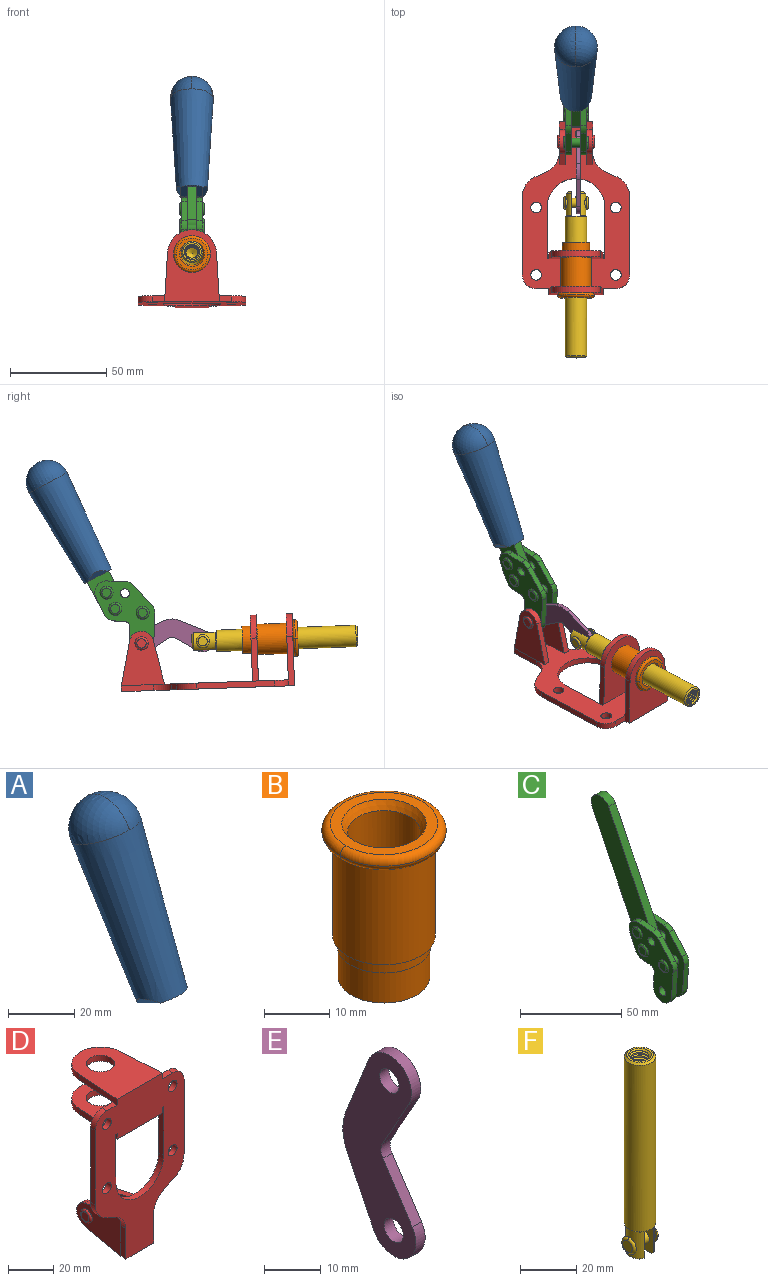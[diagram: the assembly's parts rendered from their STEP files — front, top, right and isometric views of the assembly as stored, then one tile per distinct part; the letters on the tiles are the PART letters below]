
ASSEMBLY  parts=6 mates=6
PART A: 11 faces, bbox 22.3x42.6x64.5 mm
  f0: sphere r=11.13mm, area 411.4mm2, adj f1,f8
  f1: cone r=11.11mm half-angle=3.3deg, axis (0,0.44,0.9), area 3251.8mm2, adj f0,f7,f8,f9,f10
  f2: cylinder r=6.16mm len=11.7mm, axis (1,0,0), area 89.5mm2, adj f3,f4,f5,f6
  f3: plane 60.23x36.75mm, normal (-1,0,0), area 763.6mm2, adj f2,f4,f6,f10
  f4: plane 51.37x25.05mm, normal (0,0.9,-0.44), area 264.2mm2, adj f2,f3,f5,f10
  f5: plane 60.23x36.75mm, normal (1,0,0), area 763.6mm2, adj f2,f4,f6,f10
  f6: plane 51.37x25.05mm, normal (0,-0.9,0.44), area 264.2mm2, adj f2,f3,f5,f10
  f7: plane 9.95x5.95mm, normal (0.71,-0.31,-0.64), area 25.8mm2, adj f1,f10
  f8: sphere r=11.13mm, area 411.4mm2, adj f0,f1
  f9: plane 9.95x5.95mm, normal (-0.71,-0.31,-0.64), area 25.8mm2, adj f1,f10
  f10: plane 14.27x11.38mm, normal (0,-0.44,-0.9), area 106.7mm2, adj f1,f3,f4,f5,f6,f7,f9
PART B: 15 faces, bbox 20.6x20.6x28.7 mm
  f0: torus R=8.26mm, axis (0,0,1), area 56.8mm2, adj f1,f10,f12
  f1: torus R=8.26mm, axis (0,0,1), area 56.8mm2, adj f0,f6,f13
  f2: cylinder r=5.59mm len=25.91mm, axis (0,0,1), area 909.6mm2, adj f3,f4
  f3: cone r=6.86mm half-angle=45deg, axis (0,0,-1), area 70.2mm2, adj f2,f14
  f4: cone r=6.47mm half-angle=30deg, axis (0,0,1), area 66.7mm2, adj f2,f13
  f5: cylinder r=7.04mm len=14.07mm, axis (0,0,1), area 252.6mm2, adj f11,f14
  f6: torus R=8.26mm, axis (0,0,1), area 56.8mm2, adj f1,f12,f13
  f7: cylinder r=7.16mm len=14.33mm, axis (0,0,1), area 91.5mm2, adj f9,f11
  f8: cylinder r=7.86mm len=18.42mm, axis (0,0,1), area 909.6mm2, adj f9,f10
  f9: plane 15.72x15.72mm, normal (0,0,-1), area 33mm2, adj f7,f8
  f10: plane 16.51x16.51mm, normal (0,0,-1), area 19.9mm2, adj f0,f8,f12
  f11: plane 14.33x14.33mm, normal (0,0,-1), area 5.7mm2, adj f5,f7
  f12: torus R=8.26mm, axis (0,0,1), area 56.8mm2, adj f0,f6,f10
  f13: plane 16.51x16.51mm, normal (0,0,1), area 82.7mm2, adj f1,f4,f6
  f14: plane 14.07x14.07mm, normal (0,0,-1), area 7.8mm2, adj f3,f5
PART C: 59 faces, bbox 12.9x60.2x99.6 mm
  f0: torus R=2.39mm, axis (-1,0,0), area 14.9mm2, adj f20,f43,f51
  f1: torus R=2.39mm, axis (-1,0,0), area 14.9mm2, adj f19,f42,f51
  f2: torus R=2.39mm, axis (-1,0,0), area 14.9mm2, adj f18,f35,f51
  f3: torus R=2.39mm, axis (-1,0,0), area 14.9mm2, adj f14,f17,f23
  f4: torus R=2.39mm, axis (-1,0,0), area 14.9mm2, adj f13,f16,f23
  f5: torus R=2.39mm, axis (-1,0,0), area 14.9mm2, adj f12,f15,f23
  f6: cylinder r=2.39mm len=4.78mm, axis (1,0,0), area 46.5mm2, adj f48,f50,f51
  f7: cylinder r=2.39mm len=4.78mm, axis (1,0,0), area 46.5mm2, adj f50,f51
  f8: cylinder r=6.35mm len=12.68mm, axis (1,0,0), area 61.8mm2, adj f38,f39,f50,f51
  f9: cylinder r=2.39mm len=4.78mm, axis (-1,0,0), area 70.5mm2, adj f46,f50
  f10: cylinder r=2.39mm len=4.78mm, axis (-1,0,0), area 46.5mm2, adj f23,f45,f46
  f11: cylinder r=2.39mm len=4.78mm, axis (-1,0,0), area 46.5mm2, adj f23,f46
  f12: plane 4.78x4.78mm, normal (1,0,0), area 17.9mm2, adj f5,f15
  f13: plane 4.78x4.78mm, normal (1,0,0), area 17.9mm2, adj f4,f16
  f14: plane 4.78x4.78mm, normal (1,0,0), area 17.9mm2, adj f3,f17
  f15: torus R=2.39mm, axis (-1,0,0), area 14.9mm2, adj f5,f12,f23
  f16: torus R=2.39mm, axis (-1,0,0), area 14.9mm2, adj f4,f13,f23
  f17: torus R=2.39mm, axis (-1,0,0), area 14.9mm2, adj f3,f14,f23
  f18: plane 4.78x4.78mm, normal (-1,0,0), area 17.9mm2, adj f2,f35
  f19: plane 4.78x4.78mm, normal (-1,0,0), area 17.9mm2, adj f1,f42
  f20: plane 4.78x4.78mm, normal (-1,0,0), area 17.9mm2, adj f0,f43
  f21: plane 2.26x0.2mm, normal (1,0,0), area 0.2mm2, adj f31,f44
  f22: plane 2.26x0.2mm, normal (-1,0,0), area 0.2mm2, adj f41,f44
  f23: plane 39.37x30.77mm, normal (1,0,0), area 565.5mm2, adj f3,f4,f5,f10,f11,f15,f16,f17
  f24: cylinder r=6.1mm len=4.15mm, axis (-1,0,0), area 14.7mm2, adj f23,f25,f32,f46
  f25: plane 10.25x9.01mm, normal (0,-0.75,0.66), area 42.3mm2, adj f23,f24,f26,f46
  f26: cylinder r=6.35mm len=4.64mm, axis (-1,0,0), area 15.6mm2, adj f23,f25,f27,f46
  f27: plane 15.84x3.1mm, normal (0,-1,-0.07), area 49.2mm2, adj f23,f26,f28,f46
  f28: cylinder r=6.35mm len=12.68mm, axis (-1,0,0), area 61.8mm2, adj f23,f27,f29,f46
  f29: plane 8.11x3.1mm, normal (0,1,0.07), area 25.2mm2, adj f23,f28,f30,f46
  f30: cylinder r=3.05mm len=3.25mm, axis (-1,0,0), area 14.8mm2, adj f23,f29,f31,f46
  f31: plane 5.99x3.1mm, normal (0,0.07,-1), area 18.6mm2, adj f21,f23,f30,f44,f46
  f32: plane 9.5x3.1mm, normal (0,-0.07,1), area 29.5mm2, adj f23,f24,f33,f46,f47
  f33: cylinder r=6.1mm len=8.63mm, axis (-1,0,0), area 39.1mm2, adj f23,f32,f34,f47
  f34: plane 8.65x3.96mm, normal (0,0.91,-0.42), area 29.5mm2, adj f23,f33,f44,f47
  f35: torus R=2.39mm, axis (-1,0,0), area 14.9mm2, adj f2,f18,f51
  f36: plane 10.25x9.01mm, normal (0,-0.75,0.66), area 42.3mm2, adj f37,f49,f50,f51
  f37: cylinder r=6.35mm len=4.64mm, axis (1,0,0), area 15.6mm2, adj f36,f38,f50,f51
  f38: plane 15.84x3.1mm, normal (0,-1,-0.07), area 49.2mm2, adj f8,f37,f50,f51
  f39: plane 8.11x3.1mm, normal (0,1,0.07), area 25.2mm2, adj f8,f40,f50,f51
  f40: cylinder r=3.05mm len=3.25mm, axis (1,0,0), area 14.8mm2, adj f39,f41,f50,f51
  f41: plane 5.99x3.1mm, normal (0,0.07,-1), area 18.6mm2, adj f22,f40,f44,f50,f51
  f42: torus R=2.39mm, axis (-1,0,0), area 14.9mm2, adj f1,f19,f51
  f43: torus R=2.39mm, axis (-1,0,0), area 14.9mm2, adj f0,f20,f51
  f44: cylinder r=6.35mm len=12.12mm, axis (-1,0,0), area 128.9mm2, adj f21,f22,f23,f31,f34,f41,f46,f47
  f45: plane 2.65x1.35mm, normal (1,0,0), area 1mm2, adj f10,f55
  f46: plane 39.08x20.42mm, normal (-1,0,0), area 412.5mm2, adj f9,f10,f11,f24,f25,f26,f27,f28
  f47: plane 77.62x39.82mm, normal (1,0,0), area 850mm2, adj f32,f33,f34,f44,f53,f54,f55
  f48: plane 2.65x1.35mm, normal (-1,0,0), area 1mm2, adj f6,f55
  f49: cylinder r=6.1mm len=4.15mm, axis (1,0,0), area 14.7mm2, adj f36,f50,f51,f56
  f50: plane 39.08x20.42mm, normal (1,0,0), area 412.5mm2, adj f6,f7,f8,f9,f36,f37,f38,f39
  f51: plane 39.37x30.77mm, normal (-1,0,0), area 565.5mm2, adj f0,f1,f2,f6,f7,f8,f35,f36
  f52: plane 8.65x3.96mm, normal (0,0.91,-0.42), area 29.5mm2, adj f44,f51,f57,f58
  f53: plane 68.49x33.4mm, normal (0,0.9,-0.44), area 358.1mm2, adj f44,f47,f54,f58
  f54: cylinder r=6.35mm len=12.06mm, axis (1,0,0), area 93.7mm2, adj f47,f53,f55,f58
  f55: plane 68.49x33.4mm, normal (0,-0.9,0.44), area 358.1mm2, adj f44,f45,f46,f47,f48,f50,f54,f58
  f56: plane 9.5x3.1mm, normal (0,-0.07,1), area 29.5mm2, adj f49,f50,f51,f57,f58
  f57: cylinder r=6.1mm len=8.63mm, axis (1,0,0), area 39.1mm2, adj f51,f52,f56,f58
  f58: plane 77.62x39.82mm, normal (-1,0,0), area 850mm2, adj f44,f52,f53,f54,f55,f56,f57
PART D: 55 faces, bbox 55.7x37.4x89.8 mm
  f0: torus R=2.41mm, axis (-1,0,0), area 15mm2, adj f11,f15,f25
  f1: torus R=2.41mm, axis (-1,0,0), area 15mm2, adj f10,f12,f22
  f2: cylinder r=2.78mm len=5.56mm, axis (0,-1,0), area 54.2mm2, adj f30,f54
  f3: cylinder r=14.99mm len=29.97mm, axis (0,-1,0), area 145.9mm2, adj f30,f49,f53,f54
  f4: cylinder r=2.78mm len=5.56mm, axis (0,-1,0), area 54.2mm2, adj f30,f54
  f5: cylinder r=2.78mm len=5.56mm, axis (0,-1,0), area 54.2mm2, adj f30,f54
  f6: cylinder r=2.78mm len=5.56mm, axis (0,-1,0), area 54.2mm2, adj f30,f54
  f7: cylinder r=6.35mm len=12.7mm, axis (0,0,1), area 123.6mm2, adj f27,f51
  f8: cylinder r=6.35mm len=12.7mm, axis (0,0,-1), area 124.7mm2, adj f21,f35
  f9: cylinder r=2.41mm len=11.18mm, axis (-1,0,0), area 169.4mm2, adj f16,f19
  f10: plane 4.83x4.83mm, normal (1,0,0), area 18.3mm2, adj f1,f12
  f11: plane 4.83x4.83mm, normal (-1,0,0), area 18.3mm2, adj f0,f15
  f12: torus R=2.41mm, axis (-1,0,0), area 15mm2, adj f1,f10,f22
  f13: cylinder r=6.35mm len=12.41mm, axis (1,0,0), area 53.4mm2, adj f18,f19,f22,f23
  f14: cylinder r=6.35mm len=12.41mm, axis (-1,0,0), area 53.4mm2, adj f16,f17,f24,f25
  f15: torus R=2.41mm, axis (-1,0,0), area 15mm2, adj f0,f11,f25
  f16: plane 27.86x22.35mm, normal (1,0,0), area 425.4mm2, adj f9,f14,f17,f24,f30
  f17: plane 22.86x4.97mm, normal (0,0.21,0.98), area 72.5mm2, adj f14,f16,f25,f30
  f18: plane 22.86x4.97mm, normal (0,0.21,0.98), area 72.5mm2, adj f13,f19,f22,f30
  f19: plane 27.86x22.35mm, normal (-1,0,0), area 425.4mm2, adj f9,f13,f18,f23,f30
  f20: cylinder r=12.7mm len=25.35mm, axis (0,0,-1), area 119.8mm2, adj f21,f34,f35,f36
  f21: plane 34.21x28.07mm, normal (0,0,-1), area 702.4mm2, adj f8,f20,f30,f34,f36
  f22: plane 27.96x22.45mm, normal (1,0,0), area 407.2mm2, adj f1,f12,f13,f18,f23,f30,f42,f43
  f23: plane 22.86x4.97mm, normal (0,0.21,-0.98), area 72.5mm2, adj f13,f19,f22,f44
  f24: plane 22.86x4.97mm, normal (0,0.21,-0.98), area 72.5mm2, adj f14,f16,f25,f44
  f25: plane 27.86x22.35mm, normal (-1,0,0), area 407.1mm2, adj f0,f14,f15,f17,f24,f30,f45,f46
  f26: plane 3.1x0.95mm, normal (0,0,-1), area 2.7mm2, adj f30,f49,f50,f54
  f27: plane 34.21x28.07mm, normal (0,0,1), area 702.4mm2, adj f7,f28,f30,f50,f52
  f28: cylinder r=12.7mm len=25.35mm, axis (0,0,1), area 118.8mm2, adj f27,f50,f51,f52
  f29: plane 3.1x0.95mm, normal (0,0,-1), area 2.7mm2, adj f30,f52,f53,f54
  f30: plane 86.54x55.63mm, normal (0,1,0), area 2362.9mm2, adj f2,f3,f4,f5,f6,f16,f17,f18
  f31: plane 40.56x3.1mm, normal (-1,0,0), area 125.7mm2, adj f30,f32,f48,f54
  f32: cylinder r=7.11mm len=7.11mm, axis (0,-1,0), area 34.6mm2, adj f30,f31,f33,f54
  f33: plane 6.67x3.1mm, normal (0,0,1), area 20.4mm2, adj f30,f32,f34,f54
  f34: plane 25.39x3.13mm, normal (-1,0.06,0), area 79.5mm2, adj f20,f21,f33,f35,f54
  f35: plane 37.31x28.45mm, normal (0,0,1), area 789.9mm2, adj f8,f20,f34,f36,f54
  f36: plane 25.39x3.13mm, normal (1,0.06,0), area 79.5mm2, adj f20,f21,f35,f37,f54
  f37: plane 6.67x3.1mm, normal (0,0,1), area 20.4mm2, adj f30,f36,f38,f54
  f38: cylinder r=7.11mm len=7.11mm, axis (0,-1,0), area 34.6mm2, adj f30,f37,f39,f54
  f39: plane 40.56x3.1mm, normal (1,0,0), area 125.7mm2, adj f30,f38,f40,f54
  f40: cylinder r=11.18mm len=10.16mm, axis (0,-1,0), area 39.5mm2, adj f30,f39,f41,f54
  f41: plane 6.09x3.1mm, normal (0.42,0,-0.91), area 20.8mm2, adj f30,f40,f42,f54
  f42: cylinder r=11.18mm len=9.41mm, axis (0,-1,0), area 37.2mm2, adj f22,f30,f41,f43,f54
  f43: plane 16.5x3.1mm, normal (1,0,0), area 51.1mm2, adj f22,f42,f44,f54
  f44: plane 17.37x3.1mm, normal (0,0,-1), area 53.8mm2, adj f23,f24,f30,f43,f45,f54
  f45: plane 16.5x3.1mm, normal (-1,0,0), area 51.1mm2, adj f25,f44,f46,f54
  f46: cylinder r=11.18mm len=9.41mm, axis (0,-1,0), area 37.2mm2, adj f25,f30,f45,f47,f54
  f47: plane 6.09x3.1mm, normal (-0.42,0,-0.91), area 20.8mm2, adj f30,f46,f48,f54
  f48: cylinder r=11.18mm len=10.16mm, axis (0,-1,0), area 39.5mm2, adj f30,f31,f47,f54
  f49: plane 26.54x3.1mm, normal (-1,0,0), area 82.3mm2, adj f3,f26,f30,f54
  f50: plane 25.39x3.1mm, normal (1,0.06,0), area 78.8mm2, adj f26,f27,f28,f51,f54
  f51: plane 37.31x28.45mm, normal (0,0,-1), area 789.9mm2, adj f7,f28,f50,f52,f54
  f52: plane 25.39x3.1mm, normal (-1,0.06,0), area 78.8mm2, adj f27,f28,f29,f51,f54
  f53: plane 26.54x3.1mm, normal (1,0,0), area 82.3mm2, adj f3,f29,f30,f54
  f54: plane 89.66x55.63mm, normal (0,-1,0), area 2678.5mm2, adj f2,f3,f4,f5,f6,f26,f29,f31
PART E: 12 faces, bbox 2.3x18.2x42.8 mm
  f0: cylinder r=2.4mm len=4.8mm, axis (1,0,0), area 34.9mm2, adj f4,f11
  f1: cylinder r=10.41mm len=8.47mm, axis (1,0,0), area 20.2mm2, adj f4,f9,f10,f11
  f2: cylinder r=3.05mm len=3.16mm, axis (1,0,0), area 7.7mm2, adj f4,f6,f7,f11
  f3: cylinder r=2.4mm len=4.8mm, axis (1,0,0), area 34.9mm2, adj f4,f11
  f4: plane 42.81x18.23mm, normal (-1,0,0), area 414.1mm2, adj f0,f1,f2,f3,f5,f6,f7,f8
  f5: cylinder r=5.54mm len=10.67mm, axis (1,0,0), area 41.8mm2, adj f4,f6,f10,f11
  f6: plane 11.66x6.53mm, normal (0,-0.87,-0.49), area 30.9mm2, adj f2,f4,f5,f11
  f7: plane 11.17x7.33mm, normal (0,-0.84,0.55), area 30.9mm2, adj f2,f4,f8,f11
  f8: cylinder r=5.54mm len=10.51mm, axis (1,0,0), area 41.8mm2, adj f4,f7,f9,f11
  f9: plane 13.67x6.67mm, normal (0,0.9,-0.44), area 35.1mm2, adj f1,f4,f8,f11
  f10: plane 14.1x5.7mm, normal (0,0.93,0.37), area 35.1mm2, adj f1,f4,f5,f11
  f11: plane 42.81x18.23mm, normal (1,0,0), area 414.1mm2, adj f0,f1,f2,f3,f5,f6,f7,f8
PART F: 48 faces, bbox 12.6x11.1x86.1 mm
  f0: torus R=2.41mm, axis (-1,0,0), area 15mm2, adj f30,f32,f34
  f1: torus R=2.41mm, axis (-1,0,0), area 15mm2, adj f29,f31,f33
  f2: cylinder r=5.54mm len=72.39mm, axis (0,0,1), area 2518.5mm2, adj f3,f4,f42,f43
  f3: cone r=5.54mm half-angle=45deg, axis (0,0,1), area 7.6mm2, adj f2,f5,f41
  f4: cone r=5.54mm half-angle=45deg, axis (0,0,-1), area 34.9mm2, adj f2,f39
  f5: cylinder r=5.08mm len=11.48mm, axis (0,0,1), area 108.3mm2, adj f3,f7,f8,f41
  f6: cylinder r=2.41mm len=4.83mm, axis (-1,0,0), area 71.2mm2, adj f40,f41
  f7: cylinder r=2.41mm len=4.83mm, axis (-1,0,0), area 7.6mm2, adj f5,f34
  f8: cone r=5.08mm half-angle=45deg, axis (0,0,1), area 10.6mm2, adj f5,f37,f41
  f9: cone r=3.98mm half-angle=45deg, axis (0,0,1), area 17.6mm2, adj f27,f39,f45,f46,f47
  f10: cylinder r=2.41mm len=4.83mm, axis (-1,0,0), area 7.6mm2, adj f33,f38
  f11: cylinder r=3.2mm len=6.4mm, axis (0,0,1), area 78.4mm2, adj f12,f28,f44,f45,f47
  f12: cylinder r=3.2mm len=6.4mm, axis (0,0,1), area 10.5mm2, adj f11,f13,f45,f47
  f13: cylinder r=3.2mm len=6.4mm, axis (0,0,1), area 10.5mm2, adj f12,f14,f45,f47
  f14: cylinder r=3.2mm len=6.4mm, axis (0,0,1), area 10.5mm2, adj f13,f15,f45,f47
  f15: cylinder r=3.2mm len=6.4mm, axis (0,0,1), area 10.5mm2, adj f14,f16,f45,f47
  f16: cylinder r=3.2mm len=6.4mm, axis (0,0,1), area 10.5mm2, adj f15,f17,f45,f47
  f17: cylinder r=3.2mm len=6.4mm, axis (0,0,1), area 10.5mm2, adj f16,f18,f45,f47
  f18: cylinder r=3.2mm len=6.4mm, axis (0,0,1), area 10.5mm2, adj f17,f19,f45,f47
  f19: cylinder r=3.2mm len=6.4mm, axis (0,0,1), area 10.5mm2, adj f18,f20,f45,f47
  f20: cylinder r=3.2mm len=6.4mm, axis (0,0,1), area 10.5mm2, adj f19,f21,f45,f47
  f21: cylinder r=3.2mm len=6.4mm, axis (0,0,1), area 10.5mm2, adj f20,f22,f45,f47
  f22: cylinder r=3.2mm len=6.4mm, axis (0,0,1), area 10.5mm2, adj f21,f23,f45,f47
  f23: cylinder r=3.2mm len=6.4mm, axis (0,0,1), area 10.5mm2, adj f22,f24,f45,f47
  f24: cylinder r=3.2mm len=6.4mm, axis (0,0,1), area 10.5mm2, adj f23,f25,f45,f47
  f25: cylinder r=3.2mm len=6.4mm, axis (0,0,1), area 10.5mm2, adj f24,f26,f45,f47
  f26: cylinder r=3.2mm len=6.4mm, axis (0,0,1), area 10.5mm2, adj f25,f27,f45,f47
  f27: cylinder r=3.2mm len=6.4mm, axis (0,0,1), area 7.4mm2, adj f9,f26,f45,f47
  f28: cone r=3.2mm half-angle=60deg, axis (0,0,1), area 37.2mm2, adj f11
  f29: plane 4.83x4.83mm, normal (-1,0,0), area 18.3mm2, adj f1,f31
  f30: plane 4.83x4.83mm, normal (1,0,0), area 18.3mm2, adj f0,f32
  f31: torus R=2.41mm, axis (-1,0,0), area 15mm2, adj f1,f29,f33
  f32: torus R=2.41mm, axis (-1,0,0), area 15mm2, adj f0,f30,f34
  f33: plane 6.83x6.83mm, normal (1,0,0), area 18.3mm2, adj f1,f10,f31
  f34: plane 6.83x6.83mm, normal (-1,0,0), area 18.3mm2, adj f0,f7,f32
  f35: cone r=5.08mm half-angle=45deg, axis (0,0,1), area 10.6mm2, adj f36,f38,f40
  f36: plane 7.25x1.97mm, normal (0,0,-1), area 10mm2, adj f35,f40
  f37: plane 7.25x1.97mm, normal (0,0,-1), area 10mm2, adj f8,f41
  f38: cylinder r=5.08mm len=11.48mm, axis (0,0,1), area 108.3mm2, adj f10,f35,f40,f42
  f39: plane 9.55x9.55mm, normal (0,0,1), area 22mm2, adj f4,f9
  f40: plane 12.76x10.09mm, normal (1,0,0), area 95.7mm2, adj f6,f35,f36,f38,f42,f43
  f41: plane 12.76x10.09mm, normal (-1,0,0), area 95.7mm2, adj f3,f5,f6,f8,f37,f43
  f42: cone r=5.54mm half-angle=45deg, axis (0,0,1), area 7.6mm2, adj f2,f38,f40
  f43: plane 11.07x4.7mm, normal (0,0,-1), area 50.4mm2, adj f2,f40,f41
  f44: plane 0.89x0.62mm, normal (-1,0,0), area 0.3mm2, adj f11,f45,f46,f47
  f45: bspline ~24.8x7.63mm, area 266.6mm2, adj f9,f11,f12,f13,f14,f15,f16,f17
  f46: bspline ~24.87x7.63mm, area 73.6mm2, adj f9,f44,f45,f47
  f47: bspline ~24.98x7.63mm, area 272.5mm2, adj f9,f11,f12,f13,f14,f15,f16,f17
PLACE A rot(axis=(-1,0,0),2deg) t=(-8.92,5.21,46.92)mm
PLACE B rot(axis=(1,0,0),88deg) t=(-8.88,-4.24,-9.49)mm
PLACE C rot(axis=(-1,0,0),2deg) t=(-8.88,5.21,46.92)mm
PLACE D rot(axis=(1,0,0),88deg) t=(-8.88,-4.24,-9.49)mm
PLACE E rot(axis=(1,0,0),90deg) t=(-7.73,12.43,-9.51)mm
PLACE F rot(axis=(1,0,0),88deg) t=(-8.88,11.56,-10.04)mm
MATE revolute C.f7 <-> D.f0  axis (-1,0,0) through (-8.88,28.69,13.99)mm
MATE fastened A.f2 <-> C.f54  axis (1,0,0) through (-11.23,78.12,99.19)mm
MATE revolute D.f0 <-> E.f3  axis (-1,0,0) through (-8.88,28.69,13.99)mm
MATE revolute E.f0 <-> F.f6  axis (-1,0,0) through (-8.88,-3.04,15.1)mm
MATE slider F.f2 <-> B.f12  axis (0,-1,0.03) through (-8.88,-46.32,16.61)mm
MATE fastened B.f2 <-> D.f7  axis (0,1,-0.03) through (-8.88,-49.75,16.73)mm
